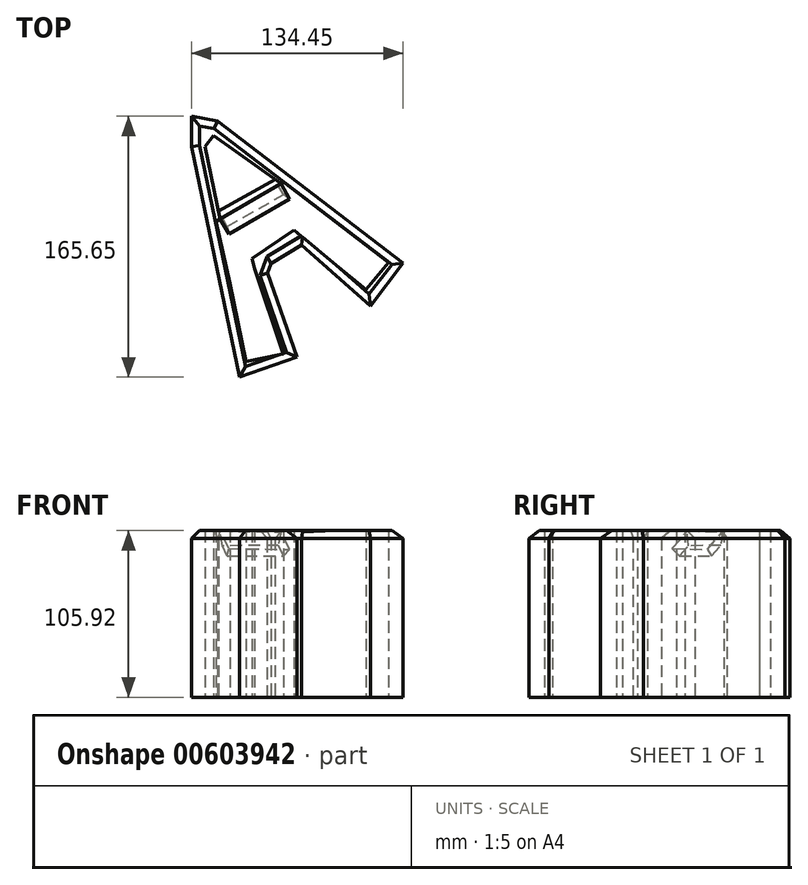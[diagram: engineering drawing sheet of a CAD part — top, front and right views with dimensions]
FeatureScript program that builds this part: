
annotation { "Feature Type Name" : "Feature", "Feature Type Description" : "" }
export const myFeature = defineFeature(function(context is Context, id is Id, definition is map)
    precondition{}
    {
        {
            var Q0;
            Q0=qCreatedBy(makeId("Top.planeOp"),FACE);
            var sketch = newSketch(context, id + "F0", { "sketchPlane" : qUnion([Q0])});
            skLineSegment(sketch, "E0", {"start": v(-58.35, 57.07) * mm, "end": v(-27.9, -89.34) * mm});
            skLineSegment(sketch, "E1", {"start": v(-27.9, -89.34) * mm, "end": v(8.55, -76.78) * mm});
            skLineSegment(sketch, "E2", {"start": v(8.55, -76.78) * mm, "end": v(-11.25, -19.3) * mm});
            skLineSegment(sketch, "E3", {"start": v(-11.25, -19.3) * mm, "end": v(11.61, -5.45) * mm});
            skLineSegment(sketch, "E4", {"start": v(11.61, -5.45) * mm, "end": v(55.26, -44.15) * mm});
            skLineSegment(sketch, "E5", {"start": v(55.26, -44.15) * mm, "end": v(76.1, -16.86) * mm});
            skLineSegment(sketch, "E6", {"start": v(76.1, -16.86) * mm, "end": v(-41.95, 73.25) * mm});
            skLineSegment(sketch, "E7", {"start": v(-41.95, 73.25) * mm, "end": v(-58.35, 76.31) * mm});
            skLineSegment(sketch, "E8", {"start": v(-58.35, 76.31) * mm, "end": v(-58.35, 57.07) * mm});
            skLineSegment(sketch, "E9", {"start": v(-33.77, -29.96) * mm, "end": v(-23.7, -79.57) * mm});
            skLineSegment(sketch, "E10", {"start": v(-23.7, -79.57) * mm, "end": v(0, -74.64) * mm});
            skLineSegment(sketch, "E11", {"start": v(0, -74.64) * mm, "end": v(-18.45, -20.55) * mm});
            skLineSegment(sketch, "E12", {"start": v(-18.45, -20.55) * mm, "end": v(-19.77, -14.2) * mm});
            skLineSegment(sketch, "E13", {"start": v(-19.77, -14.2) * mm, "end": v(6.64, 4.11) * mm});
            skLineSegment(sketch, "E14", {"start": v(6.64, 4.11) * mm, "end": v(52.58, -33.83) * mm});
            skLineSegment(sketch, "E15", {"start": v(52.58, -33.83) * mm, "end": v(66.8, -16.6) * mm});
            skLineSegment(sketch, "E16", {"start": v(66.8, -16.6) * mm, "end": v(0, 34.39) * mm});
            skLineSegment(sketch, "E17", {"start": v(0, 34.39) * mm, "end": v(-42.88, 9.46) * mm});
            skLineSegment(sketch, "E18", {"start": v(-42.88, 9.46) * mm, "end": v(-33.77, -29.96) * mm});
            skLineSegment(sketch, "E19", {"start": v(-44.34, 64.03) * mm, "end": v(-49.65, 57.07) * mm});
            skLineSegment(sketch, "E20", {"start": v(-49.65, 57.07) * mm, "end": v(-41.1, 15.94) * mm});
            skLineSegment(sketch, "E21", {"start": v(-41.1, 15.94) * mm, "end": v(-5.34, 36.22) * mm});
            skLineSegment(sketch, "E22", {"start": v(-5.34, 36.22) * mm, "end": v(-44.34, 64.03) * mm});
            skSolve(sketch);
        }
        {
            var Q0;
            Q0 = qSketchRegion(id + "F0", true);
            extrude(context, id + "F1", {"entities" : qUnion([Q0]), "depth" : 105.92 * mm, "offsetDistance" : 25.4 * mm});
        }
        {
            var Q0;
            Q0=makeQuery(id+"F1.opExtrude","CAP_EDGE",EDGE,{"disambiguationData":[OSD([sQuery(id+"F0.wireOp",EDGE,"E0")])],"isStart":false});
            var Q1;
            Q1=makeQuery(id+"F1.opExtrude","CAP_EDGE",EDGE,{"disambiguationData":[OSD([sQuery(id+"F0.wireOp",EDGE,"E8")])],"isStart":false});
            var Q2;
            Q2=makeQuery(id+"F1.opExtrude","CAP_EDGE",EDGE,{"disambiguationData":[OSD([sQuery(id+"F0.wireOp",EDGE,"E7")])],"isStart":false});
            var Q3;
            Q3=makeQuery(id+"F1.opExtrude","CAP_EDGE",EDGE,{"disambiguationData":[OSD([sQuery(id+"F0.wireOp",EDGE,"E6")])],"isStart":false});
            var Q4;
            Q4=makeQuery(id+"F1.opExtrude","CAP_EDGE",EDGE,{"disambiguationData":[OSD([sQuery(id+"F0.wireOp",EDGE,"E5")])],"isStart":false});
            var Q5;
            Q5=makeQuery(id+"F1.opExtrude","CAP_EDGE",EDGE,{"disambiguationData":[OSD([sQuery(id+"F0.wireOp",EDGE,"E4")])],"isStart":false});
            var Q6;
            Q6=makeQuery(id+"F1.opExtrude","CAP_EDGE",EDGE,{"disambiguationData":[OSD([sQuery(id+"F0.wireOp",EDGE,"E3")])],"isStart":false});
            var Q7;
            Q7=makeQuery(id+"F1.opExtrude","SWEPT_EDGE",EDGE,{"disambiguationData":[OSD([sQuery(id+"F0.wireOp",EDGE,"E2"),sQuery(id+"F0.wireOp",EDGE,"E3")])]});
            var Q8;
            Q8=makeQuery(id+"F1.opExtrude","CAP_EDGE",EDGE,{"disambiguationData":[OSD([sQuery(id+"F0.wireOp",EDGE,"E1")])],"isStart":false});
            var Q9;
            Q9=makeQuery(id+"F1.opExtrude","CAP_EDGE",EDGE,{"disambiguationData":[OSD([sQuery(id+"F0.wireOp",EDGE,"E21")])],"isStart":false});
            chamfer(context, id + "F2", {"entities" : qUnion([Q0, Q1, Q2, Q3, Q4, Q5, Q6, Q7, Q8, Q9]), "width" : 5.08 * mm, "tangentPropagation" : true});
        }
        {
            var Q0;
            Q0=makeQuery(id+"F2.opChamfer","BLEND_FACE",FACE,{"disambiguationData":[OSD([sQuery(id+"F0.wireOp",EDGE,"E21")])]});
            var sketch = newSketch(context, id + "F3", { "sketchPlane" : qUnion([Q0])});
            skSolve(sketch);
        }
        {
            var Q0;
            {var subQ0=sQuery(id+"F0.wireOp",EDGE,"E21");var subQ1=makeQuery(id+"F1.opExtrude","CAP_EDGE",EDGE,{"disambiguationData":[OSD([subQ0])],"isStart":false});Q0=makeQuery(id+"F3.imprint","IMPRINT",FACE,{"disambiguationData":[TD([[makeQuery(id+"F3.imprint","IMPRINT",EDGE,{"derivedFrom":makeQuery(id+"F2.opChamfer","BLEND_EDGE",EDGE,{"blendedFrom":[subQ1,makeQuery(id+"F1.opExtrude","SWEPT_FACE",FACE,{"disambiguationData":[OSD([sQuery(id+"F0.wireOp",EDGE,"E17")])]})],"blendedInto":[makeQuery(id+"F1.opExtrude","SWEPT_FACE",FACE,{"disambiguationData":[OSD([sQuery(id+"F0.wireOp",EDGE,"E17")])]})]})}),-1.0]])]});}
            extrude(context, id + "F4", {"entities" : qUnion([Q0]), "operationType" : NewBodyOperationType.ADD, "oppositeDirection" : true, "depth" : 15.75 * mm, "offsetDistance" : 25.4 * mm});
        }
    });
